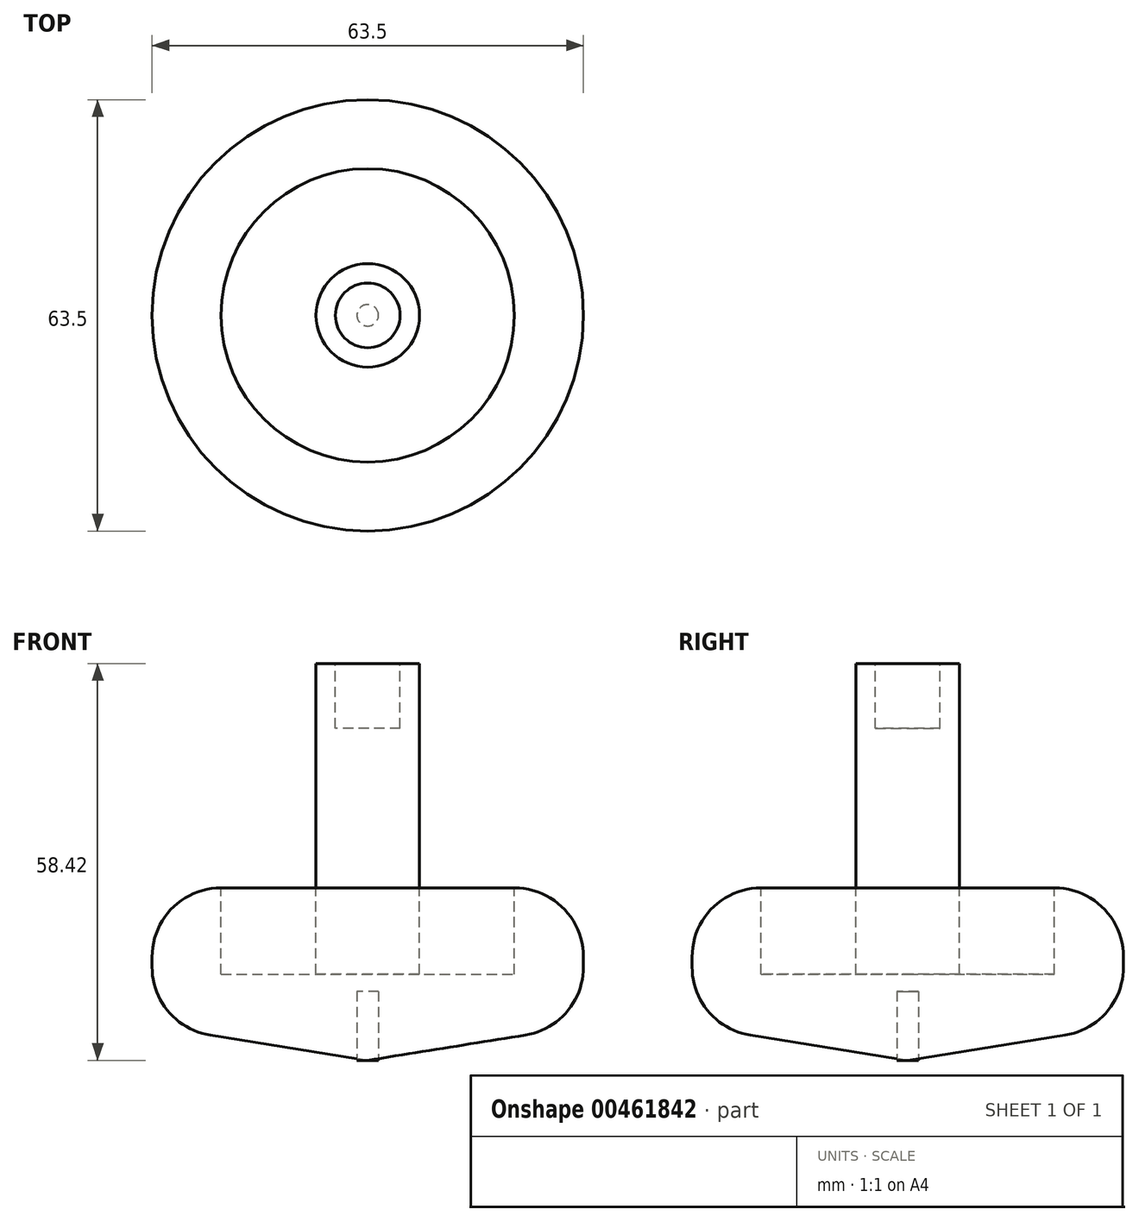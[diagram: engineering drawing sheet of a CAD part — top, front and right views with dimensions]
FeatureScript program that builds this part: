
annotation { "Feature Type Name" : "Feature", "Feature Type Description" : "" }
export const myFeature = defineFeature(function(context is Context, id is Id, definition is map)
    precondition{}
    {
        {
            var Q0;
            Q0=qCreatedBy(makeId("Front.planeOp"),FACE);
            var sketch = newSketch(context, id + "F0", { "sketchPlane" : qUnion([Q0])});
            skLineSegment(sketch, "E0", {"start": v(0, 0) * mm, "end": v(31.75, 5.08) * mm});
            skLineSegment(sketch, "E1", {"start": v(31.75, 5.08) * mm, "end": v(31.75, 25.4) * mm});
            skLineSegment(sketch, "E2", {"start": v(31.75, 25.4) * mm, "end": v(7.62, 25.4) * mm});
            skLineSegment(sketch, "E3", {"start": v(7.62, 25.4) * mm, "end": v(7.62, 58.42) * mm});
            skLineSegment(sketch, "E4", {"start": v(7.62, 58.42) * mm, "end": v(0, 58.42) * mm});
            skLineSegment(sketch, "E5", {"start": v(0, 58.42) * mm, "end": v(0, 0) * mm});
            skSolve(sketch);
        }
        {
            var Q0;
            Q0=makeQuery(id+"F0.imprint","IMPRINT",FACE,{"disambiguationData":[TD([[makeQuery(id+"F0.imprint","IMPRINT",EDGE,{"derivedFrom":sQuery(id+"F0.wireOp",EDGE,"E0")}),1.0]])]});
            var Q1;
            Q1=sQuery(id+"F0.wireOp",EDGE,"E5");
            revolve(context, id + "F1", {"entities" : qUnion([Q0]), "axis" : qUnion([Q1]), "revolveType" : RevolveType.FULL});
        }
        {
            var Q0;
            Q0=makeQuery(id+"F1.opRevolve","SWEPT_FACE",FACE,{"disambiguationData":[OSD([sQuery(id+"F0.wireOp",EDGE,"E1")])]});
            fillet(context, id + "F2", {"entities" : qUnion([Q0]), "radius" : 10.16 * mm, "tangentPropagation" : true, "allowEdgeOverflow" : false});
        }
        {
            var Q0;
            Q0=qCreatedBy(makeId("Top.planeOp"),FACE);
            var sketch = newSketch(context, id + "F3", { "sketchPlane" : qUnion([Q0])});
            skCircle(sketch, "E6", {"center": v(0, 0) * mm, "radius": 1.59 * mm});
            skSolve(sketch);
        }
        {
            var Q0;
            Q0=qSketchRegion(id+"F3",true);
            extrude(context, id + "F4", {"entities" : qUnion([Q0]), "depth" : 10.16 * mm});
        }
        {
            var Q0;
            Q0=makeQuery(id+"F1.opRevolve","SWEPT_FACE",FACE,{"disambiguationData":[OSD([sQuery(id+"F0.wireOp",EDGE,"E4")])]});
            var sketch = newSketch(context, id + "F5", { "sketchPlane" : qUnion([Q0])});
            skCircle(sketch, "E7", {"center": v(0, 0) * mm, "radius": 4.76 * mm});
            skSolve(sketch);
        }
        {
            var Q0;
            Q0=qSketchRegion(id+"F5",true);
            extrude(context, id + "F6", {"entities" : qUnion([Q0]), "oppositeDirection" : true, "depth" : 9.52 * mm});
        }
        {
            var Q0;
            Q0=makeQuery(id+"F1.opRevolve","SWEPT_FACE",FACE,{"disambiguationData":[OSD([sQuery(id+"F0.wireOp",EDGE,"E2")])]});
            extrude(context, id + "F7", {"entities" : qUnion([Q0]), "operationType" : NewBodyOperationType.REMOVE, "oppositeDirection" : true, "depth" : 12.7 * mm});
        }
    });
